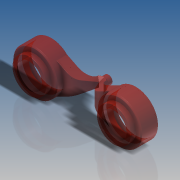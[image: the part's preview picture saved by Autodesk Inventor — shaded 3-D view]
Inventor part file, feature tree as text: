
AUTODESK INVENTOR PART (.ipt)
format: ipt  version: 2016 SP2 (Build 200236200, 236)  size: 571,904 bytes
history: native  units: in
note: dims shown in document units (in); Inventor stores cm internally (conversion verified against a paired STEP export)
features: sketch x8, extrude x3, revolve x3, mirror x3, plane x3, fillet x2, loft x1, projected_geometry x1
ambient origin geometry x8: Origin, YZ Plane, XZ Plane, XY Plane, X Axis, Y Axis, Z Axis, Center Point
bodies: Body1 (feature_tree)
feature tree (24):
  sketch  "Sketch2"  dims[d0=0.5039in d1=0.6299in]
  extrude  "Extrusion1"  Depth=0.6299in
  revolve  "Revolution2"  [1 undecoded]
  revolve  "Revolution3"  [1 undecoded]
  extrude  "Extrusion2"  Depth=0.6614in
  mirror  "Mirror2"
  extrude  "Extrusion3"  Depth=0.0157in
  plane  "Work Plane1"
  sketch  "Sketch5"  dims[d6=0.252in d7=0.6614in]
  sketch  "Sketch6"  dims[d8=45.0deg d9=0.0157in]
  plane  "Work Plane2"
  loft  "Loft1"
  mirror  "Mirror3"
  mirror  "Mirror4"
  plane  "Work Plane3"
  revolve  "Revolution4"  [1 undecoded]
  fillet  "Fillet1"  Radius=0.3937in
  fillet  "Fillet2"  Radius=0.0787in
  sketch  "Sketch3"  dims[d2=0.378in d3=0.5984in]
  sketch  "Sketch4"  dims[d4=0.189in d5=0.1417in]
  projected_geometry  "Projected Loop1"
  sketch  "Sketch7"  dims[d11=0.1732in d12=0.126in]
  sketch  "Sketch8"  dims[d13=0.1575in d14=0.1575in d15=0.3937in d16=0.0787in]
  sketch  "Sketch9"  dims[d18=0.1575in d19=0.5669in d20=0.4677in d21=0.0in d22=90.0deg d23=90.0deg d24=0.0716in d25=0.4724in d26=0.0in d27=0.063in d28=0.0in d29=-0.0315in d30=0.0in d31=90.0deg d32=0.0in d33=90.0deg d34=0.0in d35=90.0deg d36=90.0deg d37=0.0094in d38=0.0039in d39=0.0039in]
note: 3 required parameter values undecoded (feature->parameter linkage not recoverable at this tier; creation-order binding heuristic only, values carry confidence <= 0.55)
